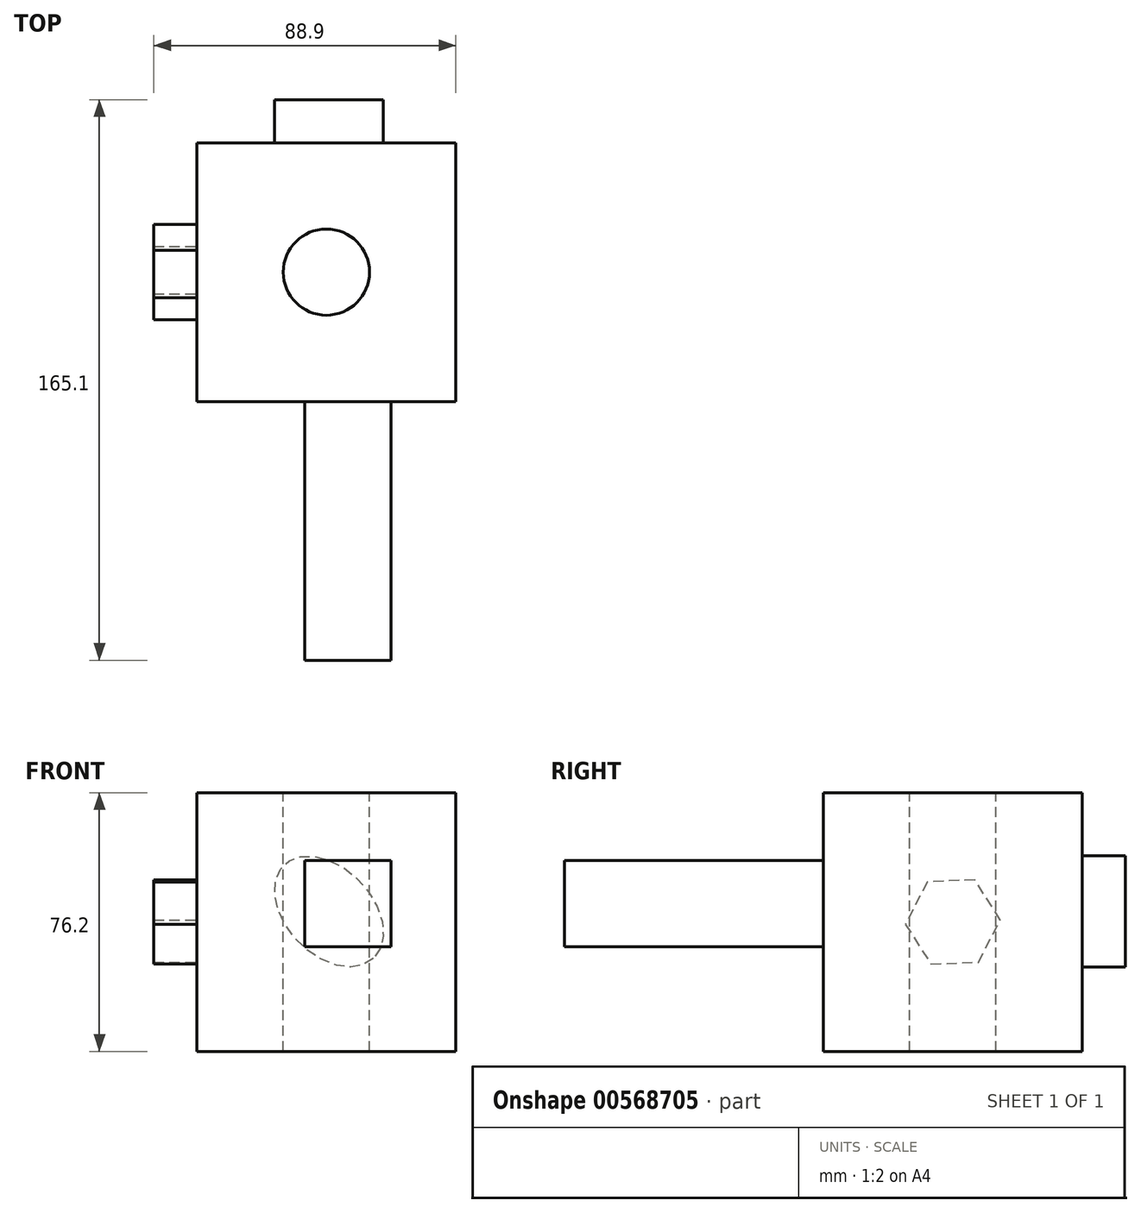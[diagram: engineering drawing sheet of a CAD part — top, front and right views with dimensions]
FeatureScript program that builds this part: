
annotation { "Feature Type Name" : "Feature", "Feature Type Description" : "" }
export const myFeature = defineFeature(function(context is Context, id is Id, definition is map)
    precondition{}
    {
        {
            var Q0;
            Q0=qCreatedBy(makeId("Front.planeOp"),FACE);
            var sketch = newSketch(context, id + "F0", { "sketchPlane" : qUnion([Q0])});
            skLineSegment(sketch, "E0.bottom", {"start": v(0, 0) * mm, "end": v(76.2, 0) * mm});
            skLineSegment(sketch, "E0.top", {"start": v(0, 76.2) * mm, "end": v(76.2, 76.2) * mm});
            skLineSegment(sketch, "E0.left", {"start": v(0, 0) * mm, "end": v(0, 76.2) * mm});
            skLineSegment(sketch, "E0.right", {"start": v(76.2, 0) * mm, "end": v(76.2, 76.2) * mm});
            skSolve(sketch);
        }
        {
            var Q0;
            Q0=makeQuery(id+"F0.imprint","IMPRINT",FACE,{"disambiguationData":[TD([[makeQuery(id+"F0.imprint","IMPRINT",EDGE,{"derivedFrom":sQuery(id+"F0.wireOp",EDGE,"E0.bottom")}),1.0]])]});
            extrude(context, id + "F1", {"entities" : qUnion([Q0]), "depth" : 76.2 * mm, "offsetDistance" : 25.4 * mm});
        }
        {
            var Q0;
            Q0=makeQuery(id+"F1.opExtrude","SWEPT_FACE",FACE,{"disambiguationData":[OSD([sQuery(id+"F0.wireOp",EDGE,"E0.top")])]});
            var sketch = newSketch(context, id + "F2", { "sketchPlane" : qUnion([Q0])});
            skPoint(sketch, "E1", {"position": v(38.1, -38.1) * mm});
            skSolve(sketch);
        }
        {
            var Q0;
            Q0=sQuery(id+"F2.wireOp",VERTEX,"E1");
            var Q1;
            Q1=makeQuery(id+"F1.opExtrude","SWEPT_BODY",BODY,{"disambiguationData":[OSD([sQuery(id+"F0.wireOp",EDGE,"E0.bottom"),sQuery(id+"F0.wireOp",EDGE,"E0.top"),sQuery(id+"F0.wireOp",EDGE,"E0.left"),sQuery(id+"F0.wireOp",EDGE,"E0.right")])]});
            hole(context, id + "F3", {"style" : HoleStyle.SIMPLE, "endStyle" : HoleEndStyle.THROUGH, "holeDiameter" : 25.4 * mm, "isTappedThrough" : true, "tappedDepth" : 12.7 * mm, "tapClearance" : 3, "locations" : qUnion([Q0]), "scope" : qUnion([Q1])});
        }
        {
            var Q0;
            Q0=makeQuery(id+"F1.opExtrude","CAP_FACE",FACE,{"disambiguationData":[OSD([sQuery(id+"F0.wireOp",EDGE,"E0.bottom"),sQuery(id+"F0.wireOp",EDGE,"E0.top"),sQuery(id+"F0.wireOp",EDGE,"E0.left"),sQuery(id+"F0.wireOp",EDGE,"E0.right")])],"isStart":false});
            var sketch = newSketch(context, id + "F4", { "sketchPlane" : qUnion([Q0])});
            skLineSegment(sketch, "E2.bottom", {"start": v(57.08, 56.26) * mm, "end": v(31.68, 56.26) * mm});
            skLineSegment(sketch, "E2.top", {"start": v(57.08, 30.86) * mm, "end": v(31.68, 30.86) * mm});
            skLineSegment(sketch, "E2.left", {"start": v(57.08, 56.26) * mm, "end": v(57.08, 30.86) * mm});
            skLineSegment(sketch, "E2.right", {"start": v(31.68, 56.26) * mm, "end": v(31.68, 30.86) * mm});
            skSolve(sketch);
        }
        {
            var Q0;
            Q0=makeQuery(id+"F4.imprint","IMPRINT",FACE,{"disambiguationData":[TD([[makeQuery(id+"F4.imprint","IMPRINT",EDGE,{"derivedFrom":sQuery(id+"F4.wireOp",EDGE,"E2.bottom")}),1.0]])]});
            extrude(context, id + "F5", {"entities" : qUnion([Q0]), "operationType" : NewBodyOperationType.ADD, "depth" : 76.2 * mm, "offsetDistance" : 25.4 * mm});
        }
        {
            var Q0;
            Q0=makeQuery(id+"F1.opExtrude","SWEPT_FACE",FACE,{"disambiguationData":[OSD([sQuery(id+"F0.wireOp",EDGE,"E0.right")])]});
            var sketch = newSketch(context, id + "F6", { "sketchPlane" : qUnion([Q0])});
            skPoint(sketch, "E3", {"position": v(-38.1, 38.1) * mm});
            skSolve(sketch);
        }
        {
            var Q0;
            {var subQ0=sQuery(id+"F0.wireOp",EDGE,"E0.right");Q0=makeQuery(id+"F6.imprint","IMPRINT",FACE,{"disambiguationData":[TD([[makeQuery(id+"F6.imprint","IMPRINT",EDGE,{"derivedFrom":makeQuery(id+"F1.opExtrude","CAP_EDGE",EDGE,{"disambiguationData":[OSD([subQ0])],"isStart":true})}),1.0]])]});}
            var sketch = newSketch(context, id + "F7", { "sketchPlane" : qUnion([Q0])});
            skPoint(sketch, "E4", {"position": v(-38.1, 38.1) * mm});
            skCircle(sketch, "E5", {"center": v(-38.1, 38.1) * mm, "radius": 12.7 * mm});
            skSolve(sketch);
        }
        {
            var Q0;
            Q0=sQuery(id+"F7.wireOp",EDGE,"E5");
            extrude(context, id + "F8", {"bodyType" : ToolBodyType.SURFACE, "surfaceEntities" : qUnion([Q0]), "depth" : 12.7 * mm, "offsetDistance" : 25.4 * mm});
        }
        {
            var Q0;
            Q0=makeQuery(id+"F1.opExtrude","SWEPT_FACE",FACE,{"disambiguationData":[OSD([sQuery(id+"F0.wireOp",EDGE,"E0.left")])]});
            var sketch = newSketch(context, id + "F9", { "sketchPlane" : qUnion([Q0])});
            skPoint(sketch, "E6", {"position": v(38.1, 38.1) * mm});
            skCircle(sketch, "E7.cCircle", {"center": v(38.1, 38.1) * mm, "radius": 12.12 * mm, "construction": true});
            skLineSegment(sketch, "E7.0", {"start": v(45.64, 49.9) * mm, "end": v(52.09, 37.47) * mm});
            skLineSegment(sketch, "E7.1", {"start": v(52.09, 37.47) * mm, "end": v(44.55, 25.67) * mm});
            skLineSegment(sketch, "E7.2", {"start": v(44.55, 25.67) * mm, "end": v(30.56, 26.3) * mm});
            skLineSegment(sketch, "E7.3", {"start": v(30.56, 26.3) * mm, "end": v(24.11, 38.73) * mm});
            skLineSegment(sketch, "E7.4", {"start": v(24.11, 38.73) * mm, "end": v(31.65, 50.53) * mm});
            skLineSegment(sketch, "E7.5", {"start": v(31.65, 50.53) * mm, "end": v(45.64, 49.9) * mm});
            skPoint(sketch, "E7.0.midPoint", {"position": v(48.86, 43.69) * mm});
            skSolve(sketch);
        }
        {
            var Q0;
            Q0 = qSketchRegion(id + "F9", true);
            extrude(context, id + "F10", {"entities" : qUnion([Q0]), "operationType" : NewBodyOperationType.ADD, "depth" : 12.7 * mm, "offsetDistance" : 25.4 * mm});
        }
        {
            var Q0;
            Q0=makeQuery(id+"F1.opExtrude","CAP_FACE",FACE,{"disambiguationData":[OSD([sQuery(id+"F0.wireOp",EDGE,"E0.bottom"),sQuery(id+"F0.wireOp",EDGE,"E0.top"),sQuery(id+"F0.wireOp",EDGE,"E0.left"),sQuery(id+"F0.wireOp",EDGE,"E0.right")])],"isStart":true});
            var sketch = newSketch(context, id + "F11", { "sketchPlane" : qUnion([Q0])});
            skPoint(sketch, "E8", {"position": v(-38.85, 41.2) * mm});
            skEllipse(sketch, "E9", {"center": v(-38.85, 41.2) * mm, "majorRadius": 12.7 * mm, "minorRadius": 19.05 * mm, "majorAxis": v(-0.72, 0.69)});
            skSolve(sketch);
        }
        {
            var Q0;
            Q0=makeQuery(id+"F11.imprint","IMPRINT",FACE,{"disambiguationData":[TD([[makeQuery(id+"F11.imprint","IMPRINT",EDGE,{"derivedFrom":sQuery(id+"F11.wireOp",EDGE,"E9")}),1.0]])]});
            extrude(context, id + "F12", {"entities" : qUnion([Q0]), "operationType" : NewBodyOperationType.ADD, "depth" : 12.7 * mm, "offsetDistance" : 25.4 * mm});
        }
    });
